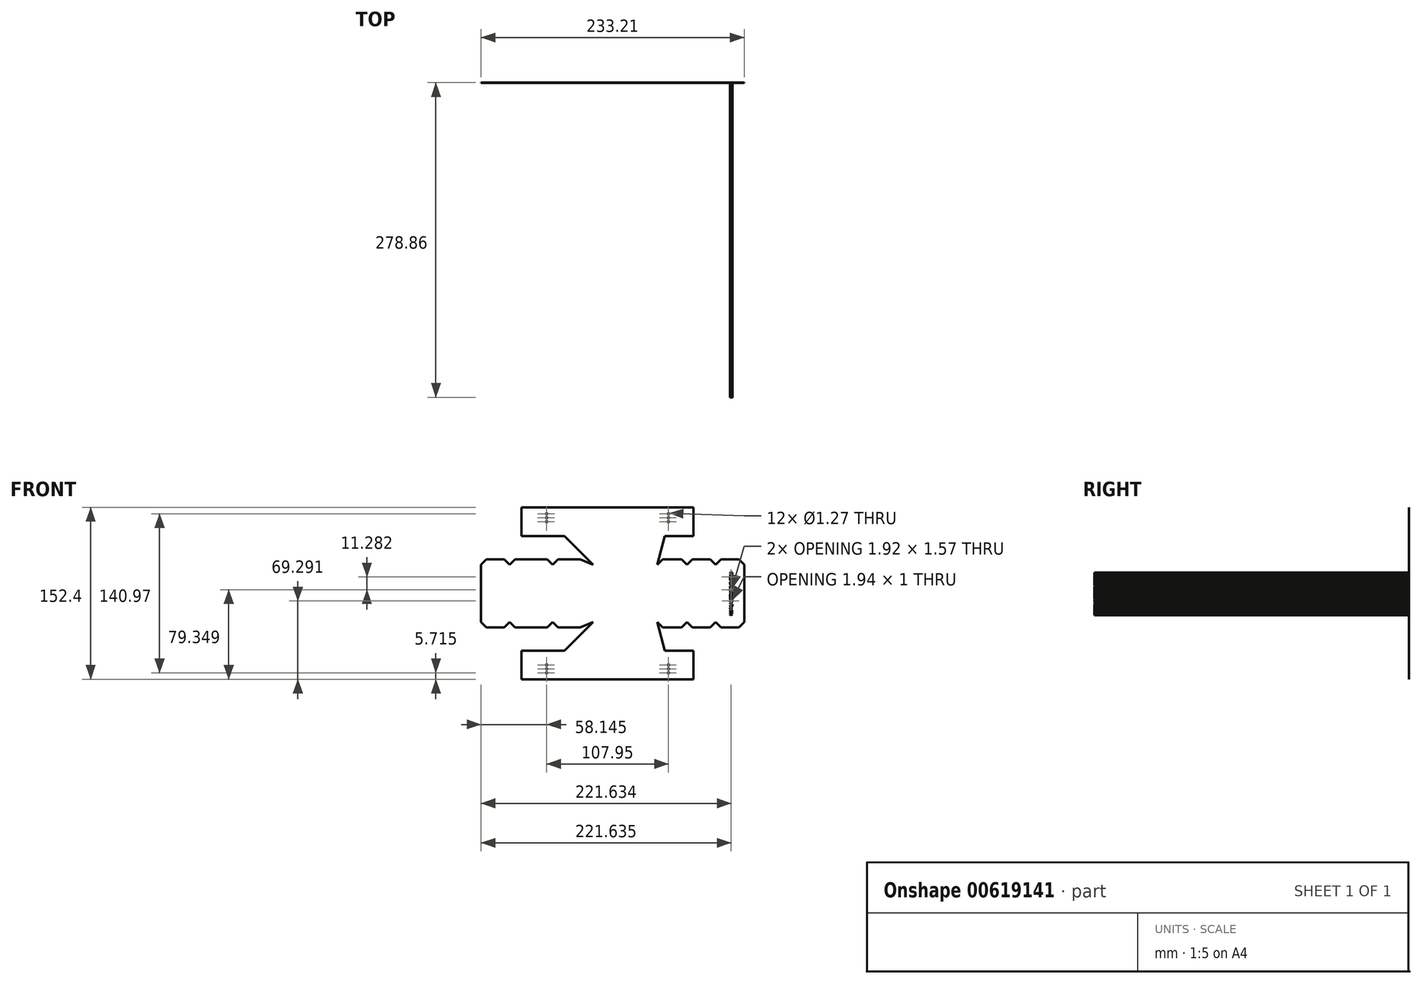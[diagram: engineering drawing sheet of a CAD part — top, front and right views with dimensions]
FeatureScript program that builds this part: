
annotation { "Feature Type Name" : "Feature", "Feature Type Description" : "" }
export const myFeature = defineFeature(function(context is Context, id is Id, definition is map)
    precondition{}
    {
        {
            var Q0;
            Q0=qCreatedBy(makeId("Front.planeOp"),FACE);
            var sketch = newSketch(context, id + "F0", { "sketchPlane" : qUnion([Q0])});
            skLineSegment(sketch, "E0", {"start": v(0, 0) * mm, "end": v(152.4, 0) * mm});
            skLineSegment(sketch, "E1", {"start": v(152.4, 0) * mm, "end": v(152.4, 25.4) * mm});
            skLineSegment(sketch, "E2", {"start": v(152.4, 25.4) * mm, "end": v(127, 25.4) * mm});
            skLineSegment(sketch, "E3", {"start": v(127, 25.4) * mm, "end": v(120.2, 50.8) * mm});
            skLineSegment(sketch, "E4", {"start": v(120.2, 50.8) * mm, "end": v(63.5, 50.8) * mm});
            skLineSegment(sketch, "E5", {"start": v(63.5, 50.8) * mm, "end": v(38.1, 25.4) * mm});
            skLineSegment(sketch, "E6", {"start": v(38.1, 25.4) * mm, "end": v(0, 25.4) * mm});
            skLineSegment(sketch, "E7", {"start": v(0, 25.4) * mm, "end": v(0, 0) * mm});
            skLineSegment(sketch, "E8", {"start": v(63.5, 50.8) * mm, "end": v(63.5, 76.2) * mm});
            skLineSegment(sketch, "E9", {"start": v(63.5, 76.2) * mm, "end": v(120.2, 76.2) * mm});
            skLineSegment(sketch, "E10", {"start": v(120.2, 76.2) * mm, "end": v(120.2, 50.8) * mm});
            skLineSegment(sketch, "E11.bottom", {"start": v(63.5, 50.8) * mm, "end": v(27.58, 50.8) * mm});
            skLineSegment(sketch, "E11.top", {"start": v(63.5, 76.2) * mm, "end": v(27.58, 76.2) * mm});
            skLineSegment(sketch, "E11.right", {"start": v(27.58, 50.8) * mm, "end": v(27.58, 76.2) * mm});
            skLineSegment(sketch, "E12.bottom", {"start": v(27.58, 76.2) * mm, "end": v(-10.52, 76.2) * mm});
            skLineSegment(sketch, "E12.top", {"start": v(27.58, 50.8) * mm, "end": v(-10.52, 50.8) * mm});
            skLineSegment(sketch, "E12.left", {"start": v(27.58, 76.2) * mm, "end": v(27.58, 50.8) * mm});
            skLineSegment(sketch, "E12.right", {"start": v(-10.52, 76.2) * mm, "end": v(-10.52, 50.8) * mm});
            skLineSegment(sketch, "E13.bottom", {"start": v(-10.52, 50.8) * mm, "end": v(-35.92, 50.8) * mm});
            skLineSegment(sketch, "E13.top", {"start": v(-10.52, 76.2) * mm, "end": v(-35.92, 76.2) * mm});
            skLineSegment(sketch, "E13.left", {"start": v(-10.52, 50.8) * mm, "end": v(-10.52, 76.2) * mm});
            skLineSegment(sketch, "E13.right", {"start": v(-35.92, 50.8) * mm, "end": v(-35.92, 76.2) * mm});
            skLineSegment(sketch, "E14.bottom", {"start": v(120.2, 76.2) * mm, "end": v(146.5, 76.2) * mm});
            skLineSegment(sketch, "E14.top", {"start": v(120.2, 50.8) * mm, "end": v(146.5, 50.8) * mm});
            skLineSegment(sketch, "E14.right", {"start": v(146.5, 76.2) * mm, "end": v(146.5, 50.8) * mm});
            skLineSegment(sketch, "E15.bottom", {"start": v(146.5, 76.2) * mm, "end": v(171.9, 76.2) * mm});
            skLineSegment(sketch, "E15.top", {"start": v(146.5, 50.8) * mm, "end": v(171.9, 50.8) * mm});
            skLineSegment(sketch, "E15.right", {"start": v(171.9, 76.2) * mm, "end": v(171.9, 50.8) * mm});
            skLineSegment(sketch, "E16.bottom", {"start": v(171.9, 76.2) * mm, "end": v(197.3, 76.2) * mm});
            skLineSegment(sketch, "E16.top", {"start": v(171.9, 50.8) * mm, "end": v(197.3, 50.8) * mm});
            skLineSegment(sketch, "E16.right", {"start": v(197.3, 76.2) * mm, "end": v(197.3, 50.8) * mm});
            skSolve(sketch);
        }
        {
            var Q0;
            Q0=qCreatedBy(makeId("Front.planeOp"),FACE);
            var sketch = newSketch(context, id + "F1", { "sketchPlane" : qUnion([Q0])});
            skLineSegment(sketch, "E17.0.0", {"start": v(-35.92, 50.8) * mm, "end": v(-10.52, 50.8) * mm});
            skLineSegment(sketch, "E17.0.1", {"start": v(-10.52, 50.8) * mm, "end": v(-10.52, 76.2) * mm});
            skLineSegment(sketch, "E17.0.2", {"start": v(-10.52, 76.2) * mm, "end": v(-35.92, 76.2) * mm});
            skLineSegment(sketch, "E17.0.3", {"start": v(-35.92, 76.2) * mm, "end": v(-35.92, 50.8) * mm});
            skLineSegment(sketch, "E18.0.0", {"start": v(27.58, 50.8) * mm, "end": v(27.58, 76.2) * mm});
            skLineSegment(sketch, "E18.0.1", {"start": v(27.58, 76.2) * mm, "end": v(-10.52, 76.2) * mm});
            skLineSegment(sketch, "E18.0.2", {"start": v(-10.52, 76.2) * mm, "end": v(-10.52, 50.8) * mm});
            skLineSegment(sketch, "E18.0.3", {"start": v(-10.52, 50.8) * mm, "end": v(27.58, 50.8) * mm});
            skLineSegment(sketch, "E19.0.0", {"start": v(63.5, 76.2) * mm, "end": v(27.58, 76.2) * mm});
            skLineSegment(sketch, "E19.0.1", {"start": v(27.58, 76.2) * mm, "end": v(27.58, 50.8) * mm});
            skLineSegment(sketch, "E19.0.2", {"start": v(27.58, 50.8) * mm, "end": v(63.5, 50.8) * mm});
            skLineSegment(sketch, "E19.0.3", {"start": v(63.5, 50.8) * mm, "end": v(63.5, 76.2) * mm});
            skLineSegment(sketch, "E20.0.0", {"start": v(120.2, 50.8) * mm, "end": v(120.2, 76.2) * mm});
            skLineSegment(sketch, "E20.0.1", {"start": v(120.2, 76.2) * mm, "end": v(63.5, 76.2) * mm});
            skLineSegment(sketch, "E20.0.2", {"start": v(63.5, 76.2) * mm, "end": v(63.5, 50.8) * mm});
            skLineSegment(sketch, "E20.0.3", {"start": v(63.5, 50.8) * mm, "end": v(120.2, 50.8) * mm});
            skLineSegment(sketch, "E21.0.0", {"start": v(146.5, 50.8) * mm, "end": v(146.5, 76.2) * mm});
            skLineSegment(sketch, "E21.0.1", {"start": v(146.5, 76.2) * mm, "end": v(120.2, 76.2) * mm});
            skLineSegment(sketch, "E21.0.2", {"start": v(120.2, 76.2) * mm, "end": v(120.2, 50.8) * mm});
            skLineSegment(sketch, "E21.0.3", {"start": v(120.2, 50.8) * mm, "end": v(146.5, 50.8) * mm});
            skLineSegment(sketch, "E22.0.0", {"start": v(171.9, 76.2) * mm, "end": v(146.5, 76.2) * mm});
            skLineSegment(sketch, "E22.0.1", {"start": v(146.5, 76.2) * mm, "end": v(146.5, 50.8) * mm});
            skLineSegment(sketch, "E22.0.2", {"start": v(146.5, 50.8) * mm, "end": v(171.9, 50.8) * mm});
            skLineSegment(sketch, "E22.0.3", {"start": v(171.9, 50.8) * mm, "end": v(171.9, 76.2) * mm});
            skLineSegment(sketch, "E23.0.0", {"start": v(197.3, 76.2) * mm, "end": v(171.9, 76.2) * mm});
            skLineSegment(sketch, "E23.0.1", {"start": v(171.9, 76.2) * mm, "end": v(171.9, 50.8) * mm});
            skLineSegment(sketch, "E23.0.2", {"start": v(171.9, 50.8) * mm, "end": v(197.3, 50.8) * mm});
            skLineSegment(sketch, "E23.0.3", {"start": v(197.3, 50.8) * mm, "end": v(197.3, 76.2) * mm});
            skLineSegment(sketch, "E24.0.0", {"start": v(38.1, 25.4) * mm, "end": v(0, 25.4) * mm});
            skLineSegment(sketch, "E24.0.1", {"start": v(0, 25.4) * mm, "end": v(0, 0) * mm});
            skLineSegment(sketch, "E24.0.2", {"start": v(0, 0) * mm, "end": v(152.4, 0) * mm});
            skLineSegment(sketch, "E24.0.3", {"start": v(152.4, 0) * mm, "end": v(152.4, 25.4) * mm});
            skLineSegment(sketch, "E24.0.4", {"start": v(152.4, 25.4) * mm, "end": v(127, 25.4) * mm});
            skLineSegment(sketch, "E24.0.5", {"start": v(127, 25.4) * mm, "end": v(120.2, 50.8) * mm});
            skLineSegment(sketch, "E24.0.6", {"start": v(120.2, 50.8) * mm, "end": v(63.5, 50.8) * mm});
            skLineSegment(sketch, "E24.0.7", {"start": v(63.5, 50.8) * mm, "end": v(38.1, 25.4) * mm});
            skLineSegment(sketch, "E25", {"start": v(-10.52, 50.8) * mm, "end": v(-15.28, 46.04) * mm});
            skLineSegment(sketch, "E26", {"start": v(-15.28, 46.04) * mm, "end": v(-31.16, 46.04) * mm});
            skLineSegment(sketch, "E27", {"start": v(-31.16, 46.04) * mm, "end": v(-35.92, 50.8) * mm});
            skLineSegment(sketch, "E28", {"start": v(-10.52, 50.8) * mm, "end": v(-5.76, 46.04) * mm});
            skLineSegment(sketch, "E29", {"start": v(-5.76, 46.04) * mm, "end": v(22.82, 46.04) * mm});
            skLineSegment(sketch, "E30", {"start": v(22.82, 46.04) * mm, "end": v(27.58, 50.8) * mm});
            skLineSegment(sketch, "E31", {"start": v(27.58, 50.8) * mm, "end": v(32.34, 46.04) * mm});
            skLineSegment(sketch, "E32", {"start": v(32.34, 46.04) * mm, "end": v(52, 46.04) * mm});
            skLineSegment(sketch, "E33", {"start": v(52, 46.04) * mm, "end": v(63.5, 50.8) * mm});
            skLineSegment(sketch, "E34", {"start": v(146.5, 50.8) * mm, "end": v(141.73, 46.04) * mm});
            skLineSegment(sketch, "E35", {"start": v(141.73, 46.04) * mm, "end": v(124.96, 46.04) * mm});
            skLineSegment(sketch, "E36", {"start": v(124.96, 46.04) * mm, "end": v(120.2, 50.8) * mm});
            skLineSegment(sketch, "E37", {"start": v(171.9, 50.8) * mm, "end": v(167.13, 46.04) * mm});
            skPoint(sketch, "E37.endSnap0", {"position": v(133.34, 46.04) * mm});
            skLineSegment(sketch, "E38", {"start": v(167.13, 46.04) * mm, "end": v(151.25, 46.04) * mm});
            skLineSegment(sketch, "E39", {"start": v(151.25, 46.04) * mm, "end": v(146.5, 50.8) * mm});
            skLineSegment(sketch, "E40", {"start": v(197.3, 50.8) * mm, "end": v(192.53, 46.04) * mm});
            skLineSegment(sketch, "E41", {"start": v(192.53, 46.04) * mm, "end": v(176.65, 46.04) * mm});
            skLineSegment(sketch, "E42", {"start": v(176.65, 46.04) * mm, "end": v(171.9, 50.8) * mm});
            skSolve(sketch);
        }
        {
            var Q0;
            Q0=makeQuery(id+"F1.imprint","IMPRINT",FACE,{"disambiguationData":[TD([[makeQuery(id+"F1.imprint","IMPRINT",EDGE,{"derivedFrom":sQuery(id+"F1.wireOp",EDGE,"E17.0.0")}),1.0]])]});
            var Q1;
            Q1=makeQuery(id+"F1.imprint","IMPRINT",FACE,{"disambiguationData":[TD([[makeQuery(id+"F1.imprint","IMPRINT",EDGE,{"derivedFrom":sQuery(id+"F1.wireOp",EDGE,"E18.0.1")}),1.0]])]});
            var Q2;
            Q2=makeQuery(id+"F1.imprint","IMPRINT",FACE,{"disambiguationData":[TD([[makeQuery(id+"F1.imprint","IMPRINT",EDGE,{"derivedFrom":sQuery(id+"F1.wireOp",EDGE,"E19.0.0")}),1.0]])]});
            var Q3;
            Q3=makeQuery(id+"F1.imprint","IMPRINT",FACE,{"disambiguationData":[TD([[makeQuery(id+"F1.imprint","IMPRINT",EDGE,{"derivedFrom":sQuery(id+"F1.wireOp",EDGE,"E20.0.1")}),1.0]])]});
            var Q4;
            Q4=makeQuery(id+"F1.imprint","IMPRINT",FACE,{"disambiguationData":[TD([[makeQuery(id+"F1.imprint","IMPRINT",EDGE,{"derivedFrom":sQuery(id+"F1.wireOp",EDGE,"E21.0.1")}),1.0]])]});
            var Q5;
            Q5=makeQuery(id+"F1.imprint","IMPRINT",FACE,{"disambiguationData":[TD([[makeQuery(id+"F1.imprint","IMPRINT",EDGE,{"derivedFrom":sQuery(id+"F1.wireOp",EDGE,"E22.0.0")}),1.0]])]});
            var Q6;
            Q6=makeQuery(id+"F1.imprint","IMPRINT",FACE,{"disambiguationData":[TD([[makeQuery(id+"F1.imprint","IMPRINT",EDGE,{"derivedFrom":sQuery(id+"F1.wireOp",EDGE,"E23.0.0")}),1.0]])]});
            var Q7;
            Q7=makeQuery(id+"F1.imprint","IMPRINT",FACE,{"disambiguationData":[TD([[makeQuery(id+"F1.imprint","IMPRINT",EDGE,{"derivedFrom":sQuery(id+"F1.wireOp",EDGE,"E24.0.0")}),1.0]])]});
            var Q8;
            Q8=makeQuery(id+"F1.imprint","IMPRINT",FACE,{"disambiguationData":[TD([[makeQuery(id+"F1.imprint","IMPRINT",EDGE,{"derivedFrom":sQuery(id+"F1.wireOp",EDGE,"E17.0.0")}),-1.0]])]});
            var Q9;
            Q9=makeQuery(id+"F1.imprint","IMPRINT",FACE,{"disambiguationData":[TD([[makeQuery(id+"F1.imprint","IMPRINT",EDGE,{"derivedFrom":sQuery(id+"F1.wireOp",EDGE,"E18.0.3")}),-1.0]])]});
            var Q10;
            Q10=makeQuery(id+"F1.imprint","IMPRINT",FACE,{"disambiguationData":[TD([[makeQuery(id+"F1.imprint","IMPRINT",EDGE,{"derivedFrom":sQuery(id+"F1.wireOp",EDGE,"E19.0.2")}),-1.0]])]});
            var Q11;
            Q11=makeQuery(id+"F1.imprint","IMPRINT",FACE,{"disambiguationData":[TD([[makeQuery(id+"F1.imprint","IMPRINT",EDGE,{"derivedFrom":sQuery(id+"F1.wireOp",EDGE,"E21.0.3")}),-1.0]])]});
            var Q12;
            Q12=makeQuery(id+"F1.imprint","IMPRINT",FACE,{"disambiguationData":[TD([[makeQuery(id+"F1.imprint","IMPRINT",EDGE,{"derivedFrom":sQuery(id+"F1.wireOp",EDGE,"E22.0.2")}),-1.0]])]});
            var Q13;
            Q13=makeQuery(id+"F1.imprint","IMPRINT",FACE,{"disambiguationData":[TD([[makeQuery(id+"F1.imprint","IMPRINT",EDGE,{"derivedFrom":sQuery(id+"F1.wireOp",EDGE,"E23.0.2")}),-1.0]])]});
            extrude(context, id + "F2", {"entities" : qUnion([Q0, Q1, Q2, Q3, Q4, Q5, Q6, Q7, Q8, Q9, Q10, Q11, Q12, Q13]), "depth" : 0.25 * mm, "offsetDistance" : 25.4 * mm});
        }
        {
            var Q0;
            Q0=makeQuery(id+"F2.opExtrude","SWEPT_BODY",BODY,{"disambiguationData":[OSD([sQuery(id+"F1.wireOp",EDGE,"E17.0.2"),sQuery(id+"F1.wireOp",EDGE,"E17.0.3"),sQuery(id+"F1.wireOp",EDGE,"E18.0.1"),sQuery(id+"F1.wireOp",EDGE,"E19.0.0"),sQuery(id+"F1.wireOp",EDGE,"E20.0.1"),sQuery(id+"F1.wireOp",EDGE,"E21.0.1"),sQuery(id+"F1.wireOp",EDGE,"E22.0.0"),sQuery(id+"F1.wireOp",EDGE,"E23.0.0"),sQuery(id+"F1.wireOp",EDGE,"E23.0.3"),sQuery(id+"F1.wireOp",EDGE,"E24.0.0"),sQuery(id+"F1.wireOp",EDGE,"E24.0.1"),sQuery(id+"F1.wireOp",EDGE,"E24.0.2"),sQuery(id+"F1.wireOp",EDGE,"E24.0.3"),sQuery(id+"F1.wireOp",EDGE,"E24.0.4"),sQuery(id+"F1.wireOp",EDGE,"E24.0.5"),sQuery(id+"F1.wireOp",EDGE,"E24.0.7"),sQuery(id+"F1.wireOp",EDGE,"E25"),sQuery(id+"F1.wireOp",EDGE,"E26"),sQuery(id+"F1.wireOp",EDGE,"E27"),sQuery(id+"F1.wireOp",EDGE,"E28"),sQuery(id+"F1.wireOp",EDGE,"E29"),sQuery(id+"F1.wireOp",EDGE,"E30"),sQuery(id+"F1.wireOp",EDGE,"E31"),sQuery(id+"F1.wireOp",EDGE,"E32"),sQuery(id+"F1.wireOp",EDGE,"E33"),sQuery(id+"F1.wireOp",EDGE,"E34"),sQuery(id+"F1.wireOp",EDGE,"E35"),sQuery(id+"F1.wireOp",EDGE,"E36"),sQuery(id+"F1.wireOp",EDGE,"E37"),sQuery(id+"F1.wireOp",EDGE,"E38"),sQuery(id+"F1.wireOp",EDGE,"E39"),sQuery(id+"F1.wireOp",EDGE,"E40"),sQuery(id+"F1.wireOp",EDGE,"E41"),sQuery(id+"F1.wireOp",EDGE,"E42")])]});
            var Q1;
            Q1=makeQuery(id+"F2.opExtrude","SWEPT_FACE",FACE,{"disambiguationData":[OSD([sQuery(id+"F1.wireOp",EDGE,"E17.0.2"),sQuery(id+"F1.wireOp",EDGE,"E18.0.1"),sQuery(id+"F1.wireOp",EDGE,"E19.0.0"),sQuery(id+"F1.wireOp",EDGE,"E20.0.1"),sQuery(id+"F1.wireOp",EDGE,"E21.0.1"),sQuery(id+"F1.wireOp",EDGE,"E22.0.0"),sQuery(id+"F1.wireOp",EDGE,"E23.0.0")])]});
            mirror(context, id + "F3", {"operationType" : NewBodyOperationType.ADD, "entities" : qUnion([Q0]), "mirrorPlane" : qUnion([Q1])});
        }
        {
            var Q0;
            {var subQ0=makeQuery(id+"F2.opExtrude","CAP_FACE",FACE,{"disambiguationData":[OSD([sQuery(id+"F1.wireOp",EDGE,"E17.0.2"),sQuery(id+"F1.wireOp",EDGE,"E17.0.3"),sQuery(id+"F1.wireOp",EDGE,"E18.0.1"),sQuery(id+"F1.wireOp",EDGE,"E19.0.0"),sQuery(id+"F1.wireOp",EDGE,"E20.0.1"),sQuery(id+"F1.wireOp",EDGE,"E21.0.1"),sQuery(id+"F1.wireOp",EDGE,"E22.0.0"),sQuery(id+"F1.wireOp",EDGE,"E23.0.0"),sQuery(id+"F1.wireOp",EDGE,"E23.0.3"),sQuery(id+"F1.wireOp",EDGE,"E24.0.0"),sQuery(id+"F1.wireOp",EDGE,"E24.0.1"),sQuery(id+"F1.wireOp",EDGE,"E24.0.2"),sQuery(id+"F1.wireOp",EDGE,"E24.0.3"),sQuery(id+"F1.wireOp",EDGE,"E24.0.4"),sQuery(id+"F1.wireOp",EDGE,"E24.0.5"),sQuery(id+"F1.wireOp",EDGE,"E24.0.7"),sQuery(id+"F1.wireOp",EDGE,"E25"),sQuery(id+"F1.wireOp",EDGE,"E26"),sQuery(id+"F1.wireOp",EDGE,"E27"),sQuery(id+"F1.wireOp",EDGE,"E28"),sQuery(id+"F1.wireOp",EDGE,"E29"),sQuery(id+"F1.wireOp",EDGE,"E30"),sQuery(id+"F1.wireOp",EDGE,"E31"),sQuery(id+"F1.wireOp",EDGE,"E32"),sQuery(id+"F1.wireOp",EDGE,"E33"),sQuery(id+"F1.wireOp",EDGE,"E34"),sQuery(id+"F1.wireOp",EDGE,"E35"),sQuery(id+"F1.wireOp",EDGE,"E36"),sQuery(id+"F1.wireOp",EDGE,"E37"),sQuery(id+"F1.wireOp",EDGE,"E38"),sQuery(id+"F1.wireOp",EDGE,"E39"),sQuery(id+"F1.wireOp",EDGE,"E40"),sQuery(id+"F1.wireOp",EDGE,"E41"),sQuery(id+"F1.wireOp",EDGE,"E42")])],"isStart":false});Q0=makeQuery(id+"F3.boolean.opBoolean","MERGE",FACE,{"derivedFrom":[subQ0,makeQuery(id+"F3.opPattern","COPY",FACE,{"derivedFrom":subQ0,"instanceName":"1"})]});}
            var sketch = newSketch(context, id + "F4", { "sketchPlane" : qUnion([Q0])});
            skCircle(sketch, "E43", {"center": v(22.22, 146.69) * mm, "radius": 0.64 * mm});
            skCircle(sketch, "E44", {"center": v(130.17, 146.69) * mm, "radius": 0.64 * mm});
            skCircle(sketch, "E45", {"center": v(130.17, 5.72) * mm, "radius": 0.64 * mm});
            skCircle(sketch, "E46", {"center": v(22.23, 5.71) * mm, "radius": 0.64 * mm});
            skCircle(sketch, "E47", {"center": v(22.22, 143.18) * mm, "radius": 0.64 * mm});
            skCircle(sketch, "E48", {"center": v(22.22, 139.7) * mm, "radius": 0.64 * mm});
            skCircle(sketch, "E49", {"center": v(130.17, 143.18) * mm, "radius": 0.64 * mm});
            skCircle(sketch, "E50", {"center": v(130.17, 139.7) * mm, "radius": 0.64 * mm});
            skCircle(sketch, "E51", {"center": v(130.18, 9.22) * mm, "radius": 0.64 * mm});
            skCircle(sketch, "E52", {"center": v(130.17, 12.7) * mm, "radius": 0.64 * mm});
            skCircle(sketch, "E53", {"center": v(22.23, 9.22) * mm, "radius": 0.64 * mm});
            skCircle(sketch, "E54", {"center": v(22.23, 12.7) * mm, "radius": 0.64 * mm});
            skLineSegment(sketch, "E55.0.0", {"start": v(-15.28, 46.04) * mm, "end": v(-10.52, 50.8) * mm});
            skLineSegment(sketch, "E55.0.1", {"start": v(-10.52, 50.8) * mm, "end": v(-5.76, 46.04) * mm});
            skLineSegment(sketch, "E55.0.2", {"start": v(-5.76, 46.04) * mm, "end": v(22.82, 46.04) * mm});
            skLineSegment(sketch, "E55.0.3", {"start": v(22.82, 46.04) * mm, "end": v(27.58, 50.8) * mm});
            skLineSegment(sketch, "E55.0.4", {"start": v(27.58, 50.8) * mm, "end": v(32.34, 46.04) * mm});
            skLineSegment(sketch, "E55.0.5", {"start": v(32.34, 46.04) * mm, "end": v(52, 46.04) * mm});
            skLineSegment(sketch, "E55.0.6", {"start": v(52, 46.04) * mm, "end": v(63.5, 50.8) * mm});
            skLineSegment(sketch, "E55.0.7", {"start": v(63.5, 50.8) * mm, "end": v(38.1, 25.4) * mm});
            skLineSegment(sketch, "E55.0.8", {"start": v(38.1, 25.4) * mm, "end": v(0, 25.4) * mm});
            skLineSegment(sketch, "E55.0.9", {"start": v(0, 25.4) * mm, "end": v(0, 0) * mm});
            skLineSegment(sketch, "E55.0.10", {"start": v(0, 0) * mm, "end": v(152.4, 0) * mm});
            skLineSegment(sketch, "E55.0.11", {"start": v(152.4, 0) * mm, "end": v(152.4, 25.4) * mm});
            skLineSegment(sketch, "E55.0.12", {"start": v(152.4, 25.4) * mm, "end": v(127, 25.4) * mm});
            skLineSegment(sketch, "E55.0.13", {"start": v(127, 25.4) * mm, "end": v(120.2, 50.8) * mm});
            skLineSegment(sketch, "E55.0.14", {"start": v(120.2, 50.8) * mm, "end": v(124.96, 46.04) * mm});
            skLineSegment(sketch, "E55.0.15", {"start": v(124.96, 46.04) * mm, "end": v(141.73, 46.04) * mm});
            skLineSegment(sketch, "E55.0.16", {"start": v(141.73, 46.04) * mm, "end": v(146.5, 50.8) * mm});
            skLineSegment(sketch, "E55.0.17", {"start": v(146.5, 50.8) * mm, "end": v(151.25, 46.04) * mm});
            skLineSegment(sketch, "E55.0.18", {"start": v(151.25, 46.04) * mm, "end": v(167.13, 46.04) * mm});
            skLineSegment(sketch, "E55.0.19", {"start": v(167.13, 46.04) * mm, "end": v(171.9, 50.8) * mm});
            skLineSegment(sketch, "E55.0.20", {"start": v(171.9, 50.8) * mm, "end": v(176.65, 46.04) * mm});
            skLineSegment(sketch, "E55.0.21", {"start": v(176.65, 46.04) * mm, "end": v(192.53, 46.04) * mm});
            skLineSegment(sketch, "E55.0.22", {"start": v(192.53, 46.04) * mm, "end": v(197.3, 50.8) * mm});
            skLineSegment(sketch, "E55.0.23", {"start": v(197.3, 50.8) * mm, "end": v(197.3, 101.6) * mm});
            skLineSegment(sketch, "E55.0.24", {"start": v(197.3, 101.6) * mm, "end": v(192.53, 106.36) * mm});
            skLineSegment(sketch, "E55.0.25", {"start": v(192.53, 106.36) * mm, "end": v(176.65, 106.36) * mm});
            skLineSegment(sketch, "E55.0.26", {"start": v(176.65, 106.36) * mm, "end": v(171.9, 101.6) * mm});
            skLineSegment(sketch, "E55.0.27", {"start": v(171.9, 101.6) * mm, "end": v(167.13, 106.36) * mm});
            skLineSegment(sketch, "E55.0.28", {"start": v(167.13, 106.36) * mm, "end": v(151.25, 106.36) * mm});
            skLineSegment(sketch, "E55.0.29", {"start": v(151.25, 106.36) * mm, "end": v(146.5, 101.6) * mm});
            skLineSegment(sketch, "E55.0.30", {"start": v(146.5, 101.6) * mm, "end": v(141.73, 106.36) * mm});
            skLineSegment(sketch, "E55.0.31", {"start": v(141.73, 106.36) * mm, "end": v(124.96, 106.36) * mm});
            skLineSegment(sketch, "E55.0.32", {"start": v(124.96, 106.36) * mm, "end": v(120.2, 101.6) * mm});
            skLineSegment(sketch, "E55.0.33", {"start": v(120.2, 101.6) * mm, "end": v(127, 127) * mm});
            skLineSegment(sketch, "E55.0.34", {"start": v(127, 127) * mm, "end": v(152.4, 127) * mm});
            skLineSegment(sketch, "E55.0.35", {"start": v(152.4, 127) * mm, "end": v(152.4, 152.4) * mm});
            skLineSegment(sketch, "E55.0.36", {"start": v(152.4, 152.4) * mm, "end": v(0, 152.4) * mm});
            skLineSegment(sketch, "E55.0.37", {"start": v(0, 152.4) * mm, "end": v(0, 127) * mm});
            skLineSegment(sketch, "E55.0.38", {"start": v(0, 127) * mm, "end": v(38.1, 127) * mm});
            skLineSegment(sketch, "E55.0.39", {"start": v(38.1, 127) * mm, "end": v(63.5, 101.6) * mm});
            skLineSegment(sketch, "E55.0.40", {"start": v(63.5, 101.6) * mm, "end": v(52, 106.36) * mm});
            skLineSegment(sketch, "E55.0.41", {"start": v(52, 106.36) * mm, "end": v(32.34, 106.36) * mm});
            skLineSegment(sketch, "E55.0.42", {"start": v(32.34, 106.36) * mm, "end": v(27.58, 101.6) * mm});
            skLineSegment(sketch, "E55.0.43", {"start": v(27.58, 101.6) * mm, "end": v(22.82, 106.36) * mm});
            skLineSegment(sketch, "E55.0.44", {"start": v(22.82, 106.36) * mm, "end": v(-5.76, 106.36) * mm});
            skLineSegment(sketch, "E55.0.45", {"start": v(-5.76, 106.36) * mm, "end": v(-10.52, 101.6) * mm});
            skLineSegment(sketch, "E55.0.46", {"start": v(-10.52, 101.6) * mm, "end": v(-15.28, 106.36) * mm});
            skLineSegment(sketch, "E55.0.47", {"start": v(-15.28, 106.36) * mm, "end": v(-31.16, 106.36) * mm});
            skLineSegment(sketch, "E55.0.48", {"start": v(-31.16, 106.36) * mm, "end": v(-35.92, 101.6) * mm});
            skLineSegment(sketch, "E55.0.49", {"start": v(-35.92, 101.6) * mm, "end": v(-35.92, 50.8) * mm});
            skLineSegment(sketch, "E55.0.50", {"start": v(-35.92, 50.8) * mm, "end": v(-31.16, 46.04) * mm});
            skLineSegment(sketch, "E55.0.51", {"start": v(-31.16, 46.04) * mm, "end": v(-15.28, 46.04) * mm});
            skSolve(sketch);
        }
        {
            var Q0;
            Q0=makeQuery(id+"F4.imprint","IMPRINT",FACE,{"disambiguationData":[TD([[makeQuery(id+"F4.imprint","IMPRINT",EDGE,{"derivedFrom":sQuery(id+"F4.wireOp",EDGE,"E43")}),1.0]])]});
            var Q1;
            Q1=makeQuery(id+"F4.imprint","IMPRINT",FACE,{"disambiguationData":[TD([[makeQuery(id+"F4.imprint","IMPRINT",EDGE,{"derivedFrom":sQuery(id+"F4.wireOp",EDGE,"E47")}),1.0]])]});
            var Q2;
            Q2=makeQuery(id+"F4.imprint","IMPRINT",FACE,{"disambiguationData":[TD([[makeQuery(id+"F4.imprint","IMPRINT",EDGE,{"derivedFrom":sQuery(id+"F4.wireOp",EDGE,"E48")}),1.0]])]});
            var Q3;
            Q3=makeQuery(id+"F4.imprint","IMPRINT",FACE,{"disambiguationData":[TD([[makeQuery(id+"F4.imprint","IMPRINT",EDGE,{"derivedFrom":sQuery(id+"F4.wireOp",EDGE,"E44")}),1.0]])]});
            var Q4;
            Q4=makeQuery(id+"F4.imprint","IMPRINT",FACE,{"disambiguationData":[TD([[makeQuery(id+"F4.imprint","IMPRINT",EDGE,{"derivedFrom":sQuery(id+"F4.wireOp",EDGE,"E49")}),1.0]])]});
            var Q5;
            Q5=makeQuery(id+"F4.imprint","IMPRINT",FACE,{"disambiguationData":[TD([[makeQuery(id+"F4.imprint","IMPRINT",EDGE,{"derivedFrom":sQuery(id+"F4.wireOp",EDGE,"E50")}),1.0]])]});
            var Q6;
            Q6=makeQuery(id+"F4.imprint","IMPRINT",FACE,{"disambiguationData":[TD([[makeQuery(id+"F4.imprint","IMPRINT",EDGE,{"derivedFrom":sQuery(id+"F4.wireOp",EDGE,"E52")}),1.0]])]});
            var Q7;
            Q7=makeQuery(id+"F4.imprint","IMPRINT",FACE,{"disambiguationData":[TD([[makeQuery(id+"F4.imprint","IMPRINT",EDGE,{"derivedFrom":sQuery(id+"F4.wireOp",EDGE,"E51")}),1.0]])]});
            var Q8;
            Q8=makeQuery(id+"F4.imprint","IMPRINT",FACE,{"disambiguationData":[TD([[makeQuery(id+"F4.imprint","IMPRINT",EDGE,{"derivedFrom":sQuery(id+"F4.wireOp",EDGE,"E45")}),1.0]])]});
            var Q9;
            Q9=makeQuery(id+"F4.imprint","IMPRINT",FACE,{"disambiguationData":[TD([[makeQuery(id+"F4.imprint","IMPRINT",EDGE,{"derivedFrom":sQuery(id+"F4.wireOp",EDGE,"E54")}),1.0]])]});
            var Q10;
            Q10=makeQuery(id+"F4.imprint","IMPRINT",FACE,{"disambiguationData":[TD([[makeQuery(id+"F4.imprint","IMPRINT",EDGE,{"derivedFrom":sQuery(id+"F4.wireOp",EDGE,"E53")}),1.0]])]});
            var Q11;
            Q11=makeQuery(id+"F4.imprint","IMPRINT",FACE,{"disambiguationData":[TD([[makeQuery(id+"F4.imprint","IMPRINT",EDGE,{"derivedFrom":sQuery(id+"F4.wireOp",EDGE,"E46")}),1.0]])]});
            extrude(context, id + "F5", {"entities" : qUnion([Q0, Q1, Q2, Q3, Q4, Q5, Q6, Q7, Q8, Q9, Q10, Q11]), "operationType" : NewBodyOperationType.REMOVE, "endBound" : BoundingType.THROUGH_ALL, "oppositeDirection" : true, "depth" : 25.4 * mm, "offsetDistance" : 25.4 * mm});
        }
        {
            var Q0;
            {var subQ0=makeQuery(id+"F2.opExtrude","CAP_FACE",FACE,{"disambiguationData":[OSD([sQuery(id+"F1.wireOp",EDGE,"E17.0.2"),sQuery(id+"F1.wireOp",EDGE,"E17.0.3"),sQuery(id+"F1.wireOp",EDGE,"E18.0.1"),sQuery(id+"F1.wireOp",EDGE,"E19.0.0"),sQuery(id+"F1.wireOp",EDGE,"E20.0.1"),sQuery(id+"F1.wireOp",EDGE,"E21.0.1"),sQuery(id+"F1.wireOp",EDGE,"E22.0.0"),sQuery(id+"F1.wireOp",EDGE,"E23.0.0"),sQuery(id+"F1.wireOp",EDGE,"E23.0.3"),sQuery(id+"F1.wireOp",EDGE,"E24.0.0"),sQuery(id+"F1.wireOp",EDGE,"E24.0.1"),sQuery(id+"F1.wireOp",EDGE,"E24.0.2"),sQuery(id+"F1.wireOp",EDGE,"E24.0.3"),sQuery(id+"F1.wireOp",EDGE,"E24.0.4"),sQuery(id+"F1.wireOp",EDGE,"E24.0.5"),sQuery(id+"F1.wireOp",EDGE,"E24.0.7"),sQuery(id+"F1.wireOp",EDGE,"E25"),sQuery(id+"F1.wireOp",EDGE,"E26"),sQuery(id+"F1.wireOp",EDGE,"E27"),sQuery(id+"F1.wireOp",EDGE,"E28"),sQuery(id+"F1.wireOp",EDGE,"E29"),sQuery(id+"F1.wireOp",EDGE,"E30"),sQuery(id+"F1.wireOp",EDGE,"E31"),sQuery(id+"F1.wireOp",EDGE,"E32"),sQuery(id+"F1.wireOp",EDGE,"E33"),sQuery(id+"F1.wireOp",EDGE,"E34"),sQuery(id+"F1.wireOp",EDGE,"E35"),sQuery(id+"F1.wireOp",EDGE,"E36"),sQuery(id+"F1.wireOp",EDGE,"E37"),sQuery(id+"F1.wireOp",EDGE,"E38"),sQuery(id+"F1.wireOp",EDGE,"E39"),sQuery(id+"F1.wireOp",EDGE,"E40"),sQuery(id+"F1.wireOp",EDGE,"E41"),sQuery(id+"F1.wireOp",EDGE,"E42")])],"isStart":false});Q0=makeQuery(id+"F3.boolean.opBoolean","MERGE",FACE,{"derivedFrom":[subQ0,makeQuery(id+"F3.opPattern","COPY",FACE,{"derivedFrom":subQ0,"instanceName":"1"})]});}
            var sketch = newSketch(context, id + "F6", { "sketchPlane" : qUnion([Q0])});
            skText(sketch, "E56", { "text": "WWW.10BITWORKS.COM", "fontName": "OpenSans-Regular.ttf"});
            const initialGuessF6  = {"E56": [0.18688, 0.05656, 0, 1, 0.00235]};
            skSetInitialGuess(sketch, initialGuessF6);
            skSolve(sketch);
        }
        {
            var Q0;
            Q0 = qSketchRegion(id + "F6", true);
            extrude(context, id + "F7", {"entities" : qUnion([Q0]), "endBound" : BoundingType.THROUGH_ALL, "depth" : 25.4 * mm, "offsetDistance" : 25.4 * mm});
        }
    });
